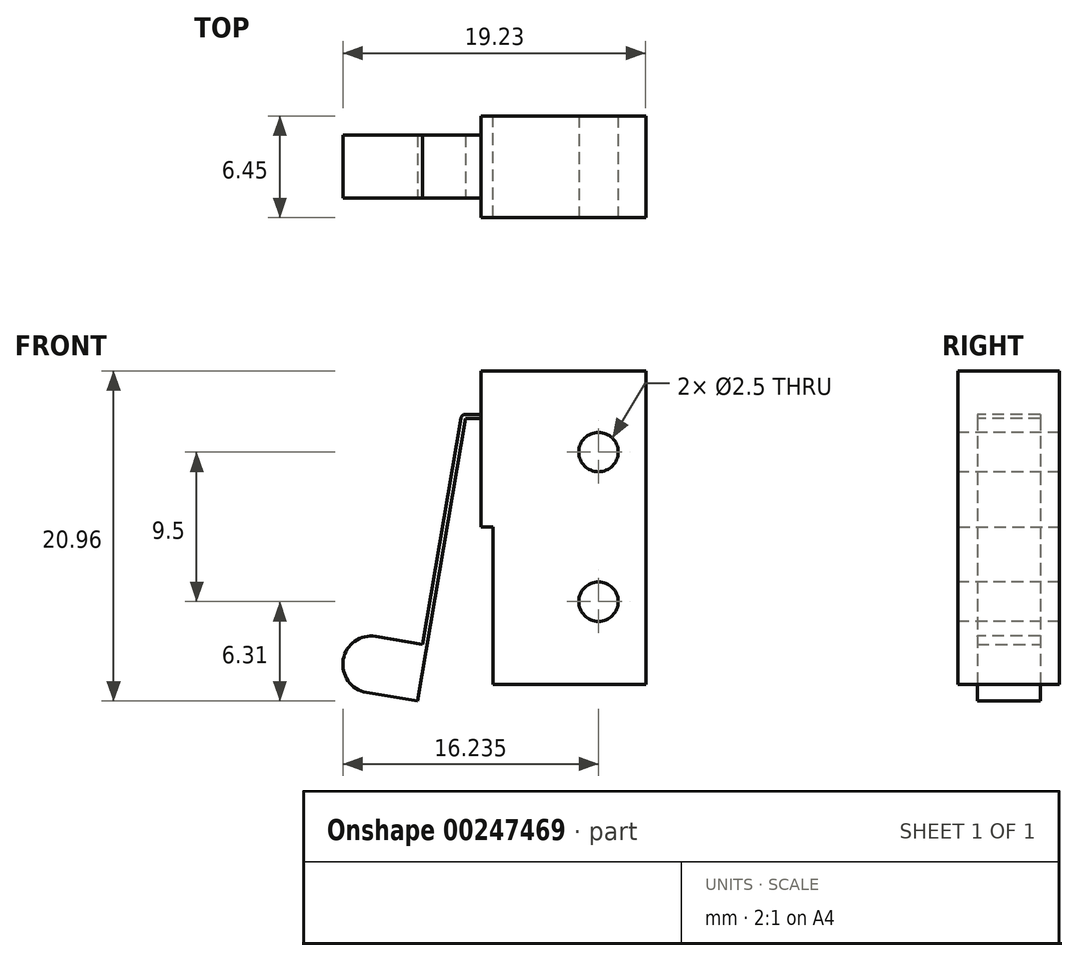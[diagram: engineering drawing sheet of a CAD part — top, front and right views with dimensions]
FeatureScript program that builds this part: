
annotation { "Feature Type Name" : "Feature", "Feature Type Description" : "" }
export const myFeature = defineFeature(function(context is Context, id is Id, definition is map)
    precondition{}
    {
        {
            var Q0;
            Q0=qCreatedBy(makeId("Front.planeOp"),FACE);
            var sketch = newSketch(context, id + "F0", { "sketchPlane" : qUnion([Q0])});
            skLineSegment(sketch, "E0.bottom", {"start": v(-5.22, -9.95) * mm, "end": v(5.23, -9.95) * mm});
            skLineSegment(sketch, "E0.top", {"start": v(-5.23, 9.95) * mm, "end": v(5.22, 9.95) * mm});
            skLineSegment(sketch, "E0.left", {"start": v(-5.22, -9.95) * mm, "end": v(-5.23, 9.95) * mm});
            skLineSegment(sketch, "E0.right", {"start": v(5.23, -9.95) * mm, "end": v(5.22, 9.95) * mm});
            skPoint(sketch, "E0.middle", {"position": v(0, 0) * mm});
            skSolve(sketch);
        }
        {
            var Q0;
            Q0 = qSketchRegion(id + "F0", true);
            extrude(context, id + "F1", {"entities" : qUnion([Q0]), "depth" : 6.45 * mm});
        }
        {
            var Q0;
            Q0=makeQuery(id+"F1.opExtrude","SWEPT_FACE",FACE,{"disambiguationData":[OSD([sQuery(id+"F0.wireOp",EDGE,"E0.left")])]});
            var sketch = newSketch(context, id + "F2", { "sketchPlane" : qUnion([Q0])});
            skLineSegment(sketch, "E1.bottom", {"start": v(6.45, -9.95) * mm, "end": v(0, -9.95) * mm});
            skLineSegment(sketch, "E1.top", {"start": v(6.45, 0.05) * mm, "end": v(0, 0.05) * mm});
            skLineSegment(sketch, "E1.left", {"start": v(6.45, -9.95) * mm, "end": v(6.45, 0.05) * mm});
            skLineSegment(sketch, "E1.right", {"start": v(0, -9.95) * mm, "end": v(0, 0.05) * mm});
            skSolve(sketch);
        }
        {
            var Q0;
            Q0 = qSketchRegion(id + "F2", true);
            extrude(context, id + "F3", {"entities" : qUnion([Q0]), "operationType" : NewBodyOperationType.REMOVE, "oppositeDirection" : true, "depth" : .75 * mm});
        }
        {
            var Q0;
            Q0=makeQuery(id+"F1.opExtrude","SWEPT_FACE",FACE,{"disambiguationData":[OSD([sQuery(id+"F0.wireOp",EDGE,"E0.left")])]});
            var sketch = newSketch(context, id + "F4", { "sketchPlane" : qUnion([Q0])});
            skLineSegment(sketch, "E2.bottom", {"start": v(1.23, 7.2) * mm, "end": v(5.23, 7.2) * mm});
            skLineSegment(sketch, "E2.top", {"start": v(1.23, 6.92) * mm, "end": v(5.23, 6.92) * mm});
            skLineSegment(sketch, "E2.left", {"start": v(1.23, 7.2) * mm, "end": v(1.23, 6.92) * mm});
            skLineSegment(sketch, "E2.right", {"start": v(5.23, 7.2) * mm, "end": v(5.23, 6.92) * mm});
            skSolve(sketch);
        }
        {
            var Q0;
            Q0 = qSketchRegion(id + "F4", true);
            extrude(context, id + "F5", {"entities" : qUnion([Q0]), "operationType" : NewBodyOperationType.ADD, "depth" : 1 * mm});
        }
        {
            var Q0;
            Q0=makeQuery(id+"F5.opExtrude","SWEPT_FACE",FACE,{"disambiguationData":[OSD([sQuery(id+"F4.wireOp",EDGE,"E2.right")])]});
            var sketch = newSketch(context, id + "F6", { "sketchPlane" : qUnion([Q0])});
            skLineSegment(sketch, "E3", {"start": v(-6.23, 6.92) * mm, "end": v(-9.28, -11.01) * mm});
            skLineSegment(sketch, "E4.0", {"start": v(-6.5, 6.97) * mm, "end": v(-9.56, -10.97) * mm});
            skArc(sketch, "E5", {"start": v(-6.5, 6.97) * mm, "mid": v(-6.4, 7.13) * mm, "end": v(-6.23, 7.2) * mm});
            skLineSegment(sketch, "E6", {"start": v(-9.28, -11.01) * mm, "end": v(-9.56, -10.97) * mm});
            skLineSegment(sketch, "E7", {"start": v(-6.23, 6.92) * mm, "end": v(-6.23, 7.2) * mm});
            skSolve(sketch);
        }
        {
            var Q0;
            Q0 = qSketchRegion(id + "F6", true);
            extrude(context, id + "F7", {"entities" : qUnion([Q0]), "operationType" : NewBodyOperationType.ADD, "oppositeDirection" : true, "depth" : 4 * mm});
        }
        {
            var Q0;
            Q0=makeQuery(id+"F7.opExtrude","SWEPT_FACE",FACE,{"disambiguationData":[OSD([sQuery(id+"F6.wireOp",EDGE,"E4.0")])]});
            var sketch = newSketch(context, id + "F8", { "sketchPlane" : qUnion([Q0])});
            skLineSegment(sketch, "E8.bottom", {"start": v(5.23, -12.42) * mm, "end": v(1.23, -12.42) * mm});
            skLineSegment(sketch, "E8.top", {"start": v(5.23, -8.82) * mm, "end": v(1.23, -8.82) * mm});
            skLineSegment(sketch, "E8.left", {"start": v(5.23, -12.42) * mm, "end": v(5.23, -8.82) * mm});
            skLineSegment(sketch, "E8.right", {"start": v(1.23, -12.42) * mm, "end": v(1.23, -8.82) * mm});
            skSolve(sketch);
        }
        {
            var Q0;
            Q0 = qSketchRegion(id + "F8", true);
            extrude(context, id + "F9", {"entities" : qUnion([Q0]), "operationType" : NewBodyOperationType.ADD, "depth" : 4.8 * mm});
        }
        {
            var Q0;
            Q0=makeQuery(id+"F1.opExtrude","CAP_FACE",FACE,{"disambiguationData":[OSD([sQuery(id+"F0.wireOp",EDGE,"E0.bottom"),sQuery(id+"F0.wireOp",EDGE,"E0.top"),sQuery(id+"F0.wireOp",EDGE,"E0.left"),sQuery(id+"F0.wireOp",EDGE,"E0.right")])],"isStart":false});
            var sketch = newSketch(context, id + "F10", { "sketchPlane" : qUnion([Q0])});
            skPoint(sketch, "E9", {"position": v(2.23, -4.7) * mm});
            skPoint(sketch, "E10", {"position": v(2.22, 4.8) * mm});
            skSolve(sketch);
        }
        {
            var Q0;
            Q0=sQuery(id+"F10.wireOp",VERTEX,"E9");
            var Q1;
            Q1=sQuery(id+"F10.wireOp",VERTEX,"E10");
            var Q2;
            Q2=makeQuery(id+"F1.opExtrude","SWEPT_BODY",BODY,{"disambiguationData":[OSD([sQuery(id+"F0.wireOp",EDGE,"E0.bottom"),sQuery(id+"F0.wireOp",EDGE,"E0.top"),sQuery(id+"F0.wireOp",EDGE,"E0.left"),sQuery(id+"F0.wireOp",EDGE,"E0.right")])]});
            hole(context, id + "F11", {"style" : HoleStyle.SIMPLE, "endStyle" : HoleEndStyle.THROUGH, "holeDiameter" : 2.5 * mm, "tappedDepth" : 12 * mm, "tapClearance" : 3, "locations" : qUnion([Q0, Q1]), "scope" : qUnion([Q2])});
        }
        {
            var Q0;
            Q0=makeQuery(id+"F9.boolean.opBoolean","MERGE",FACE,{"derivedFrom":[makeQuery(id+"F7.boolean.opBoolean","MERGE",FACE,{"derivedFrom":[makeQuery(id+"F5.opExtrude","SWEPT_FACE",FACE,{"disambiguationData":[OSD([sQuery(id+"F4.wireOp",EDGE,"E2.right")])]}),makeQuery(id+"F7.opExtrude","CAP_FACE",FACE,{"disambiguationData":[OSD([sQuery(id+"F6.wireOp",EDGE,"E3"),sQuery(id+"F6.wireOp",EDGE,"E4.0"),sQuery(id+"F6.wireOp",EDGE,"E5"),sQuery(id+"F6.wireOp",EDGE,"E6"),sQuery(id+"F6.wireOp",EDGE,"E7")])],"isStart":true})]}),makeQuery(id+"F9.opExtrude","SWEPT_FACE",FACE,{"disambiguationData":[OSD([sQuery(id+"F8.wireOp",EDGE,"E8.left")])]})]});
            var sketch = newSketch(context, id + "F12", { "sketchPlane" : qUnion([Q0])});
            skLineSegment(sketch, "E11.0", {"start": v(-12.21, -8.69) * mm, "end": v(-12.52, -10.46) * mm, "construction": true});
            skLineSegment(sketch, "E12", {"start": v(-12.21, -8.69) * mm, "end": v(-15.85, -8.07) * mm, "construction": true});
            skLineSegment(sketch, "E13", {"start": v(-14.3, -10.16) * mm, "end": v(-13.69, -6.61) * mm});
            skLineSegment(sketch, "E14", {"start": v(-13.69, -6.61) * mm, "end": v(-11.91, -6.91) * mm});
            skLineSegment(sketch, "E15", {"start": v(-12.52, -10.46) * mm, "end": v(-14.3, -10.16) * mm});
            skArc(sketch, "E16", {"start": v(-11.91, -6.91) * mm, "mid": v(-13.99, -8.39) * mm, "end": v(-12.52, -10.46) * mm});
            skSolve(sketch);
        }
        {
            var Q0;
            Q0 = qSketchRegion(id + "F12", true);
            extrude(context, id + "F13", {"entities" : qUnion([Q0]), "operationType" : NewBodyOperationType.REMOVE, "endBound" : BoundingType.UP_TO_NEXT, "oppositeDirection" : true, "depth" : 25 * mm});
        }
    });
